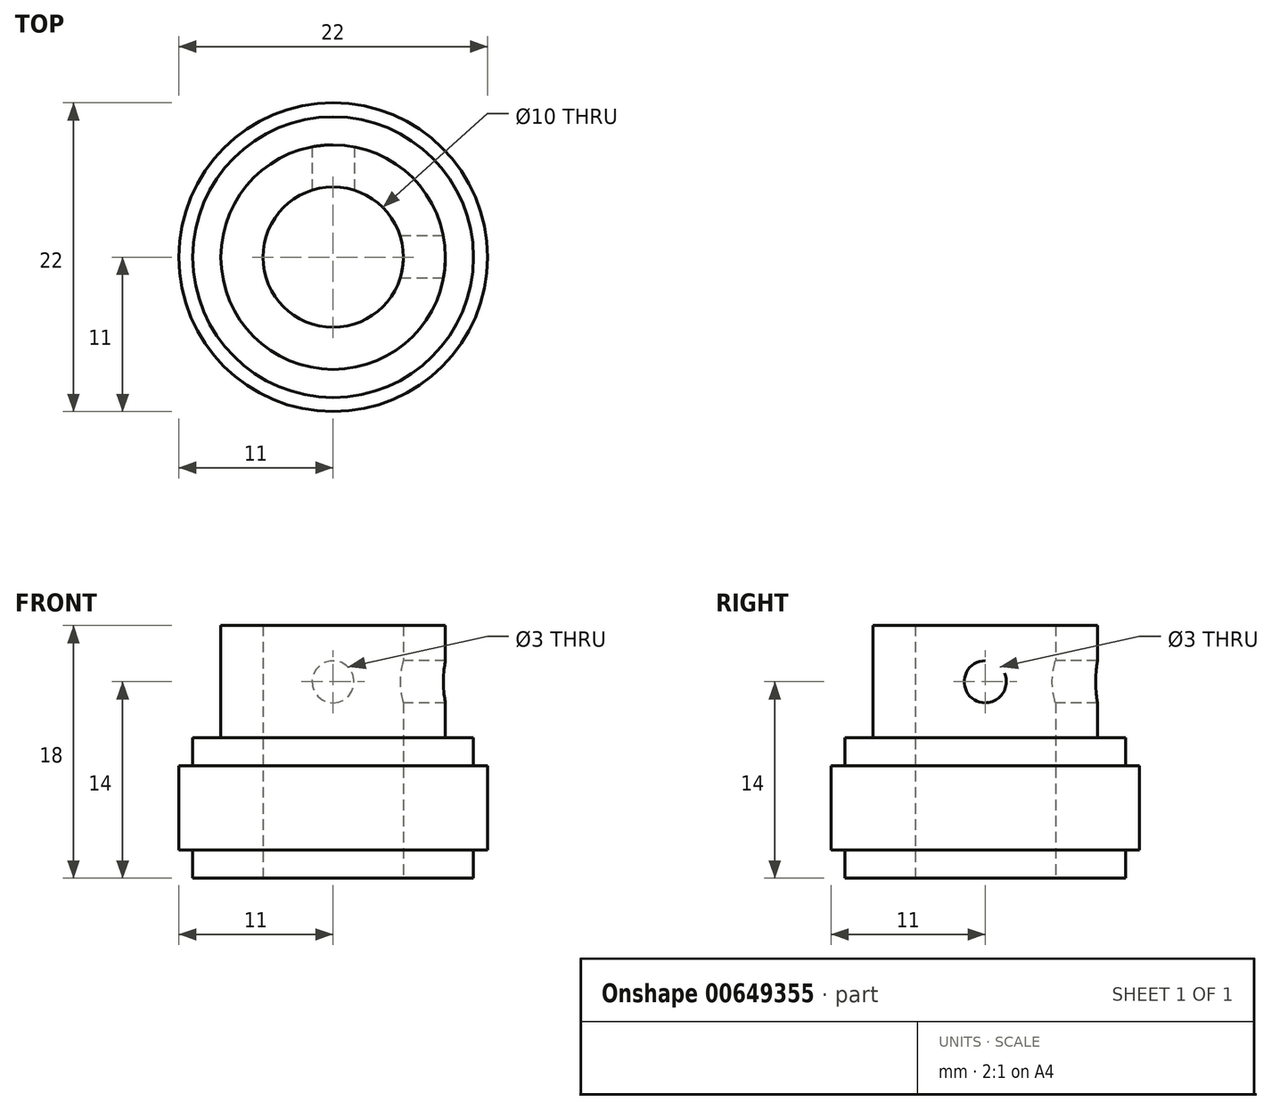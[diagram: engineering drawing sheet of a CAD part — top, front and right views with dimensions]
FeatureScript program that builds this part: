
annotation { "Feature Type Name" : "Feature", "Feature Type Description" : "" }
export const myFeature = defineFeature(function(context is Context, id is Id, definition is map)
    precondition{}
    {
        {
            var Q0;
            Q0=qCreatedBy(makeId("Top.planeOp"),FACE);
            var sketch = newSketch(context, id + "F0", { "sketchPlane" : qUnion([Q0])});
            skCircle(sketch, "E0", {"center": v(0, 0) * mm, "radius": 5 * mm});
            skCircle(sketch, "E1", {"center": v(0, 0) * mm, "radius": 10 * mm});
            skCircle(sketch, "E2", {"center": v(0, 0) * mm, "radius": 11 * mm});
            skCircle(sketch, "E3", {"center": v(0, 0) * mm, "radius": 8 * mm});
            skSolve(sketch);
        }
        {
            var Q0;
            Q0=qCreatedBy(makeId("Right.planeOp"),FACE);
            var sketch = newSketch(context, id + "F1", { "sketchPlane" : qUnion([Q0])});
            skCircle(sketch, "E4", {"center": v(0, 14) * mm, "radius": 1.5 * mm});
            skSolve(sketch);
        }
        {
            var Q0;
            Q0=makeQuery(id+"F0.imprint","IMPRINT",FACE,{"disambiguationData":[TD([[makeQuery(id+"F0.imprint","IMPRINT",EDGE,{"derivedFrom":sQuery(id+"F0.wireOp",EDGE,"E0")}),-1.0]])]});
            extrude(context, id + "F2", {"entities" : qUnion([Q0]), "depth" : 18 * mm, "offsetDistance" : 25 * mm});
        }
        {
            var Q0;
            Q0=makeQuery(id+"F0.imprint","IMPRINT",FACE,{"disambiguationData":[TD([[makeQuery(id+"F0.imprint","IMPRINT",EDGE,{"derivedFrom":sQuery(id+"F0.wireOp",EDGE,"E1")}),1.0]])]});
            extrude(context, id + "F3", {"entities" : qUnion([Q0]), "operationType" : NewBodyOperationType.ADD, "depth" : 10 * mm, "offsetDistance" : 25 * mm});
        }
        {
            var Q0;
            Q0=makeQuery(id+"F0.imprint","IMPRINT",FACE,{"disambiguationData":[TD([[makeQuery(id+"F0.imprint","IMPRINT",EDGE,{"derivedFrom":sQuery(id+"F0.wireOp",EDGE,"E1")}),-1.0]])]});
            extrude(context, id + "F4", {"entities" : qUnion([Q0]), "operationType" : NewBodyOperationType.ADD, "depth" : 8 * mm, "offsetDistance" : 25 * mm, "hasSecondDirection" : true, "secondDirectionOppositeDirection" : false, "secondDirectionDepth" : 2 * mm});
        }
        {
            var Q0;
            Q0 = qSketchRegion(id + "F1", true);
            extrude(context, id + "F5", {"entities" : qUnion([Q0]), "operationType" : NewBodyOperationType.REMOVE, "endBound" : BoundingType.THROUGH_ALL, "depth" : 25 * mm, "offsetDistance" : 25 * mm});
        }
        {
            var Q0;
            Q0=qCreatedBy(makeId("Front.planeOp"),FACE);
            var sketch = newSketch(context, id + "F6", { "sketchPlane" : qUnion([Q0])});
            skCircle(sketch, "E5", {"center": v(0, 14) * mm, "radius": 1.5 * mm});
            skSolve(sketch);
        }
        {
            var Q0;
            Q0 = qSketchRegion(id + "F6", true);
            extrude(context, id + "F7", {"entities" : qUnion([Q0]), "operationType" : NewBodyOperationType.REMOVE, "endBound" : BoundingType.THROUGH_ALL, "oppositeDirection" : true, "depth" : 25 * mm, "offsetDistance" : 25 * mm});
        }
    });
